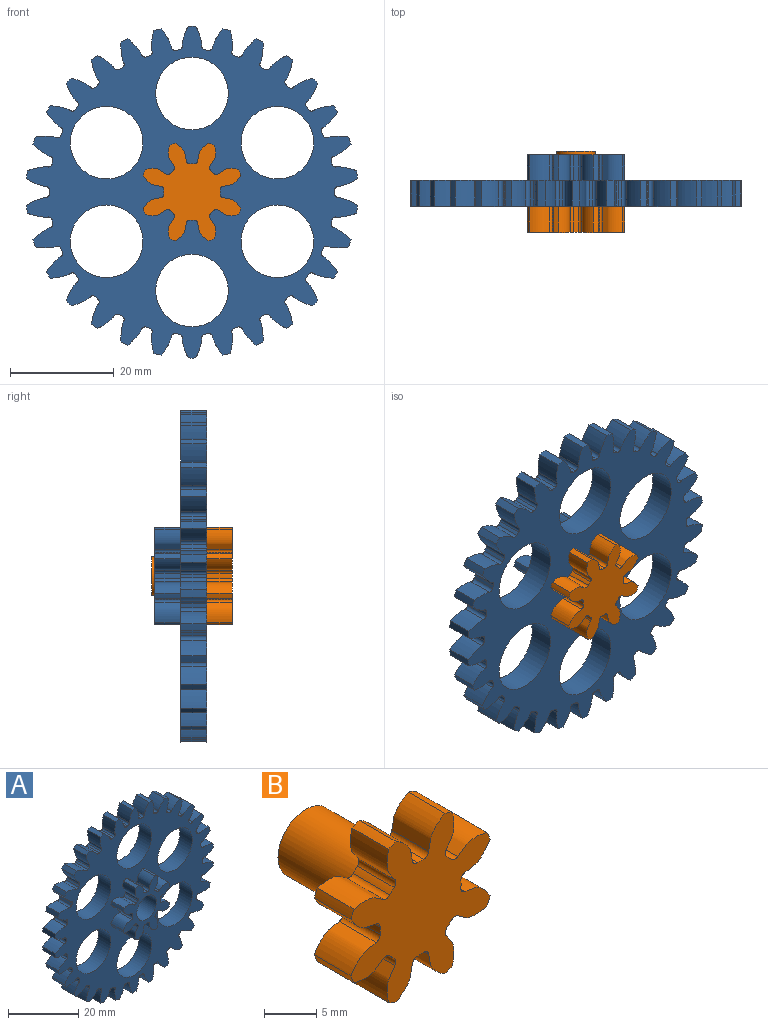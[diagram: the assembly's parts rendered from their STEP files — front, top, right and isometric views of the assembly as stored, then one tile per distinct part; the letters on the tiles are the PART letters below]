
ASSEMBLY  parts=2 mates=1
PART A: 238 faces, bbox 63.8x10x64 mm
  f0: extruded ~5x3.41mm, area 21.2mm2, adj f31,f32,f33,f49
  f1: cylinder r=5.5mm len=5mm, axis (0,1,0), area 4.1mm2, adj f32,f33,f34,f49
  f2: extruded ~5x3.41mm, area 21.2mm2, adj f3,f32,f34,f49
  f3: cylinder r=10mm len=5mm, axis (0,1,0), area 5.4mm2, adj f2,f4,f32,f49
  f4: extruded ~5x3.98mm, area 21.2mm2, adj f3,f32,f35,f49
  f5: cylinder r=5.5mm len=5mm, axis (0,1,0), area 4.1mm2, adj f32,f35,f36,f49
  f6: extruded ~5x3.98mm, area 21.2mm2, adj f7,f32,f36,f49
  f7: cylinder r=10mm len=5mm, axis (0,1,0), area 5.4mm2, adj f6,f8,f32,f49
  f8: extruded ~5x3.41mm, area 21.2mm2, adj f7,f32,f37,f49
  f9: cylinder r=5.5mm len=5mm, axis (0,1,0), area 4.1mm2, adj f32,f37,f38,f49
  f10: extruded ~5x3.41mm, area 21.2mm2, adj f11,f32,f38,f49
  f11: cylinder r=10mm len=5mm, axis (0,1,0), area 5.4mm2, adj f10,f12,f32,f49
  f12: extruded ~5x3.98mm, area 21.2mm2, adj f11,f32,f39,f49
  f13: cylinder r=5.5mm len=5mm, axis (0,1,0), area 4.1mm2, adj f32,f39,f40,f49
  f14: extruded ~5x3.98mm, area 21.2mm2, adj f15,f32,f40,f49
  f15: cylinder r=10mm len=5mm, axis (0,1,0), area 5.4mm2, adj f14,f16,f32,f49
  f16: extruded ~5x3.41mm, area 21.2mm2, adj f15,f32,f41,f49
  f17: cylinder r=5.5mm len=5mm, axis (0,1,0), area 4.1mm2, adj f32,f41,f42,f49
  f18: extruded ~5x3.41mm, area 21.2mm2, adj f19,f32,f42,f49
  f19: cylinder r=10mm len=5mm, axis (0,1,0), area 5.4mm2, adj f18,f20,f32,f49
  f20: extruded ~5x3.98mm, area 21.2mm2, adj f19,f32,f43,f49
  f21: cylinder r=5.5mm len=5mm, axis (0,1,0), area 4.1mm2, adj f32,f43,f44,f49
  f22: extruded ~5x3.98mm, area 21.2mm2, adj f23,f32,f44,f49
  f23: cylinder r=10mm len=5mm, axis (0,1,0), area 5.4mm2, adj f22,f24,f32,f49
  f24: extruded ~5x3.41mm, area 21.2mm2, adj f23,f32,f45,f49
  f25: cylinder r=5.5mm len=5mm, axis (0,1,0), area 4.1mm2, adj f32,f45,f46,f49
  f26: extruded ~5x3.41mm, area 21.2mm2, adj f27,f32,f46,f49
  f27: cylinder r=10mm len=5mm, axis (0,1,0), area 5.4mm2, adj f26,f28,f32,f49
  f28: extruded ~5x3.98mm, area 21.2mm2, adj f27,f32,f47,f49
  f29: cylinder r=5.5mm len=5mm, axis (0,1,0), area 4.1mm2, adj f32,f47,f48,f49
  f30: extruded ~5x3.98mm, area 21.2mm2, adj f31,f32,f48,f49
  f31: cylinder r=10mm len=5mm, axis (0,1,0), area 5.4mm2, adj f0,f30,f32,f49
  f32: plane 18.97x18.97mm, normal (0,-1,0), area 140mm2, adj f0,f1,f2,f3,f4,f5,f6,f7
  f33: cylinder r=0.66mm len=5mm, axis (0,1,0), area 4.8mm2, adj f0,f1,f32,f49
  f34: cylinder r=0.66mm len=5mm, axis (0,1,0), area 4.8mm2, adj f1,f2,f32,f49
  f35: cylinder r=0.66mm len=5mm, axis (0,1,0), area 4.8mm2, adj f4,f5,f32,f49
  f36: cylinder r=0.66mm len=5mm, axis (0,1,0), area 4.8mm2, adj f5,f6,f32,f49
  f37: cylinder r=0.66mm len=5mm, axis (0,1,0), area 4.8mm2, adj f8,f9,f32,f49
  f38: cylinder r=0.66mm len=5mm, axis (0,1,0), area 4.8mm2, adj f9,f10,f32,f49
  f39: cylinder r=0.66mm len=5mm, axis (0,1,0), area 4.8mm2, adj f12,f13,f32,f49
  f40: cylinder r=0.66mm len=5mm, axis (0,1,0), area 4.8mm2, adj f13,f14,f32,f49
  f41: cylinder r=0.66mm len=5mm, axis (0,1,0), area 4.8mm2, adj f16,f17,f32,f49
  f42: cylinder r=0.66mm len=5mm, axis (0,1,0), area 4.8mm2, adj f17,f18,f32,f49
  f43: cylinder r=0.66mm len=5mm, axis (0,1,0), area 4.8mm2, adj f20,f21,f32,f49
  f44: cylinder r=0.66mm len=5mm, axis (0,1,0), area 4.8mm2, adj f21,f22,f32,f49
  f45: cylinder r=0.66mm len=5mm, axis (0,1,0), area 4.8mm2, adj f24,f25,f32,f49
  f46: cylinder r=0.66mm len=5mm, axis (0,1,0), area 4.8mm2, adj f25,f26,f32,f49
  f47: cylinder r=0.66mm len=5mm, axis (0,1,0), area 4.8mm2, adj f28,f29,f32,f49
  f48: cylinder r=0.66mm len=5mm, axis (0,1,0), area 4.8mm2, adj f29,f30,f32,f49
  f49: plane 64x63.79mm, normal (0,-1,0), area 1681.1mm2, adj f0,f1,f2,f3,f4,f5,f6,f7
  f50: extruded ~5x3.75mm, area 20.5mm2, adj f49,f169,f170,f230
  f51: cylinder r=27.5mm len=5mm, axis (0,1,0), area 3.6mm2, adj f49,f170,f171,f230
  f52: extruded ~5x3.75mm, area 20.5mm2, adj f49,f53,f171,f230
  f53: cylinder r=32mm len=5mm, axis (0,1,0), area 7.4mm2, adj f49,f52,f54,f230
  f54: extruded ~5x3.99mm, area 20.5mm2, adj f49,f53,f172,f230
  f55: cylinder r=27.5mm len=5mm, axis (0,1,0), area 3.6mm2, adj f49,f172,f173,f230
  f56: extruded ~5x3.34mm, area 20.5mm2, adj f49,f57,f173,f230
  f57: cylinder r=32mm len=5mm, axis (0,1,0), area 7.4mm2, adj f49,f56,f58,f230
  f58: extruded ~5x4.06mm, area 20.5mm2, adj f49,f57,f174,f230
  f59: cylinder r=27.5mm len=5mm, axis (0,1,0), area 3.6mm2, adj f49,f174,f175,f230
  f60: extruded ~5x2.95mm, area 20.5mm2, adj f49,f61,f175,f230
  f61: cylinder r=32mm len=5mm, axis (0,1,0), area 7.4mm2, adj f49,f60,f62,f230
  f62: extruded ~5x3.95mm, area 20.5mm2, adj f49,f61,f176,f230
  f63: cylinder r=27.5mm len=5mm, axis (0,1,0), area 3.6mm2, adj f49,f176,f177,f230
  f64: extruded ~5x3.46mm, area 20.5mm2, adj f49,f65,f177,f230
  f65: cylinder r=32mm len=5mm, axis (0,1,0), area 7.4mm2, adj f49,f64,f66,f230
  f66: extruded ~5x3.67mm, area 20.5mm2, adj f49,f65,f178,f230
  f67: cylinder r=27.5mm len=5mm, axis (0,1,0), area 3.6mm2, adj f49,f178,f179,f230
  f68: extruded ~5x3.83mm, area 20.5mm2, adj f49,f69,f179,f230
  f69: cylinder r=32mm len=5mm, axis (0,1,0), area 7.4mm2, adj f49,f68,f70,f230
  f70: extruded ~5x3.22mm, area 20.5mm2, adj f49,f69,f180,f230
  f71: cylinder r=27.5mm len=5mm, axis (0,1,0), area 3.6mm2, adj f49,f180,f181,f230
  f72: extruded ~5x4.02mm, area 20.5mm2, adj f49,f73,f181,f230
  f73: cylinder r=32mm len=5mm, axis (0,1,0), area 7.4mm2, adj f49,f72,f74,f230
  f74: extruded ~5x3.08mm, area 20.5mm2, adj f49,f73,f182,f230
  f75: cylinder r=27.5mm len=5mm, axis (0,1,0), area 3.6mm2, adj f49,f182,f183,f230
  f76: extruded ~5x4.04mm, area 20.5mm2, adj f49,f77,f183,f230
  f77: cylinder r=32mm len=5mm, axis (0,1,0), area 7.4mm2, adj f49,f76,f78,f230
  f78: extruded ~5x3.56mm, area 20.5mm2, adj f49,f77,f184,f230
  f79: cylinder r=27.5mm len=5mm, axis (0,1,0), area 3.6mm2, adj f49,f184,f185,f230
  f80: extruded ~5x3.89mm, area 20.5mm2, adj f49,f81,f185,f230
  f81: cylinder r=32mm len=5mm, axis (0,1,0), area 7.4mm2, adj f49,f80,f82,f230
  f82: extruded ~5x3.89mm, area 20.5mm2, adj f49,f81,f186,f230
  f83: cylinder r=27.5mm len=5mm, axis (0,1,0), area 3.6mm2, adj f49,f186,f187,f230
  f84: extruded ~5x3.56mm, area 20.5mm2, adj f49,f85,f187,f230
  f85: cylinder r=32mm len=5mm, axis (0,1,0), area 7.4mm2, adj f49,f84,f86,f230
  f86: extruded ~5x4.04mm, area 20.5mm2, adj f49,f85,f188,f230
  f87: cylinder r=27.5mm len=5mm, axis (0,1,0), area 3.6mm2, adj f49,f188,f189,f230
  f88: extruded ~5x3.08mm, area 20.5mm2, adj f49,f89,f189,f230
  f89: cylinder r=32mm len=5mm, axis (0,1,0), area 7.4mm2, adj f49,f88,f90,f230
  f90: extruded ~5x4.02mm, area 20.5mm2, adj f49,f89,f190,f230
  f91: cylinder r=27.5mm len=5mm, axis (0,1,0), area 3.6mm2, adj f49,f190,f191,f230
  f92: extruded ~5x3.22mm, area 20.5mm2, adj f49,f93,f191,f230
  f93: cylinder r=32mm len=5mm, axis (0,1,0), area 7.4mm2, adj f49,f92,f94,f230
  f94: extruded ~5x3.83mm, area 20.5mm2, adj f49,f93,f192,f230
  f95: cylinder r=27.5mm len=5mm, axis (0,1,0), area 3.6mm2, adj f49,f192,f193,f230
  f96: extruded ~5x3.67mm, area 20.5mm2, adj f49,f97,f193,f230
  f97: cylinder r=32mm len=5mm, axis (0,1,0), area 7.4mm2, adj f49,f96,f98,f230
  f98: extruded ~5x3.46mm, area 20.5mm2, adj f49,f97,f194,f230
  f99: cylinder r=27.5mm len=5mm, axis (0,1,0), area 3.6mm2, adj f49,f194,f195,f230
  f100: extruded ~5x3.95mm, area 20.5mm2, adj f49,f101,f195,f230
  f101: cylinder r=32mm len=5mm, axis (0,1,0), area 7.4mm2, adj f49,f100,f102,f230
  f102: extruded ~5x2.95mm, area 20.5mm2, adj f49,f101,f196,f230
  f103: cylinder r=27.5mm len=5mm, axis (0,1,0), area 3.6mm2, adj f49,f196,f197,f230
  f104: extruded ~5x4.06mm, area 20.5mm2, adj f49,f105,f197,f230
  f105: cylinder r=32mm len=5mm, axis (0,1,0), area 7.4mm2, adj f49,f104,f106,f230
  f106: extruded ~5x3.34mm, area 20.5mm2, adj f49,f105,f198,f230
  f107: cylinder r=27.5mm len=5mm, axis (0,1,0), area 3.6mm2, adj f49,f198,f199,f230
  f108: extruded ~5x3.99mm, area 20.5mm2, adj f49,f109,f199,f230
  f109: cylinder r=32mm len=5mm, axis (0,1,0), area 7.4mm2, adj f49,f108,f110,f230
  f110: extruded ~5x3.75mm, area 20.5mm2, adj f49,f109,f200,f230
  f111: cylinder r=27.5mm len=5mm, axis (0,1,0), area 3.6mm2, adj f49,f200,f201,f230
  f112: extruded ~5x3.75mm, area 20.5mm2, adj f49,f113,f201,f230
  f113: cylinder r=32mm len=5mm, axis (0,1,0), area 7.4mm2, adj f49,f112,f114,f230
  f114: extruded ~5x3.99mm, area 20.5mm2, adj f49,f113,f202,f230
  f115: cylinder r=27.5mm len=5mm, axis (0,1,0), area 3.6mm2, adj f49,f202,f203,f230
  f116: extruded ~5x3.34mm, area 20.5mm2, adj f49,f117,f203,f230
  f117: cylinder r=32mm len=5mm, axis (0,1,0), area 7.4mm2, adj f49,f116,f118,f230
  f118: extruded ~5x4.06mm, area 20.5mm2, adj f49,f117,f204,f230
  f119: cylinder r=27.5mm len=5mm, axis (0,1,0), area 3.6mm2, adj f49,f204,f205,f230
  f120: extruded ~5x2.95mm, area 20.5mm2, adj f49,f121,f205,f230
  f121: cylinder r=32mm len=5mm, axis (0,1,0), area 7.4mm2, adj f49,f120,f122,f230
  f122: extruded ~5x3.95mm, area 20.5mm2, adj f49,f121,f206,f230
  f123: cylinder r=27.5mm len=5mm, axis (0,1,0), area 3.6mm2, adj f49,f206,f207,f230
  f124: extruded ~5x3.46mm, area 20.5mm2, adj f49,f125,f207,f230
  f125: cylinder r=32mm len=5mm, axis (0,1,0), area 7.4mm2, adj f49,f124,f126,f230
  f126: extruded ~5x3.67mm, area 20.5mm2, adj f49,f125,f208,f230
  f127: cylinder r=27.5mm len=5mm, axis (0,1,0), area 3.6mm2, adj f49,f208,f209,f230
  f128: extruded ~5x3.83mm, area 20.5mm2, adj f49,f129,f209,f230
  f129: cylinder r=32mm len=5mm, axis (0,1,0), area 7.4mm2, adj f49,f128,f130,f230
  f130: extruded ~5x3.22mm, area 20.5mm2, adj f49,f129,f210,f230
  f131: cylinder r=27.5mm len=5mm, axis (0,1,0), area 3.6mm2, adj f49,f210,f211,f230
  f132: extruded ~5x4.02mm, area 20.5mm2, adj f49,f133,f211,f230
  f133: cylinder r=32mm len=5mm, axis (0,1,0), area 7.4mm2, adj f49,f132,f134,f230
  f134: extruded ~5x3.08mm, area 20.5mm2, adj f49,f133,f212,f230
  f135: cylinder r=27.5mm len=5mm, axis (0,1,0), area 3.6mm2, adj f49,f212,f213,f230
  f136: extruded ~5x4.04mm, area 20.5mm2, adj f49,f137,f213,f230
  f137: cylinder r=32mm len=5mm, axis (0,1,0), area 7.4mm2, adj f49,f136,f138,f230
  f138: extruded ~5x3.56mm, area 20.5mm2, adj f49,f137,f214,f230
  f139: cylinder r=27.5mm len=5mm, axis (0,1,0), area 3.6mm2, adj f49,f214,f215,f230
  f140: extruded ~5x3.89mm, area 20.5mm2, adj f49,f141,f215,f230
  f141: cylinder r=32mm len=5mm, axis (0,1,0), area 7.4mm2, adj f49,f140,f142,f230
  f142: extruded ~5x3.89mm, area 20.5mm2, adj f49,f141,f216,f230
  f143: cylinder r=27.5mm len=5mm, axis (0,1,0), area 3.6mm2, adj f49,f216,f217,f230
  f144: extruded ~5x3.56mm, area 20.5mm2, adj f49,f145,f217,f230
  f145: cylinder r=32mm len=5mm, axis (0,1,0), area 7.4mm2, adj f49,f144,f146,f230
  f146: extruded ~5x4.04mm, area 20.5mm2, adj f49,f145,f218,f230
  f147: cylinder r=27.5mm len=5mm, axis (0,1,0), area 3.6mm2, adj f49,f218,f219,f230
  f148: extruded ~5x3.08mm, area 20.5mm2, adj f49,f149,f219,f230
  f149: cylinder r=32mm len=5mm, axis (0,1,0), area 7.4mm2, adj f49,f148,f150,f230
  f150: extruded ~5x4.02mm, area 20.5mm2, adj f49,f149,f220,f230
  f151: cylinder r=27.5mm len=5mm, axis (0,1,0), area 3.6mm2, adj f49,f220,f221,f230
  f152: extruded ~5x3.22mm, area 20.5mm2, adj f49,f153,f221,f230
  f153: cylinder r=32mm len=5mm, axis (0,1,0), area 7.4mm2, adj f49,f152,f154,f230
  f154: extruded ~5x3.83mm, area 20.5mm2, adj f49,f153,f222,f230
  f155: cylinder r=27.5mm len=5mm, axis (0,1,0), area 3.6mm2, adj f49,f222,f223,f230
  f156: extruded ~5x3.67mm, area 20.5mm2, adj f49,f157,f223,f230
  f157: cylinder r=32mm len=5mm, axis (0,1,0), area 7.4mm2, adj f49,f156,f158,f230
  f158: extruded ~5x3.46mm, area 20.5mm2, adj f49,f157,f224,f230
  f159: cylinder r=27.5mm len=5mm, axis (0,1,0), area 3.6mm2, adj f49,f224,f225,f230
  f160: extruded ~5x3.95mm, area 20.5mm2, adj f49,f161,f225,f230
  f161: cylinder r=32mm len=5mm, axis (0,1,0), area 7.4mm2, adj f49,f160,f162,f230
  f162: extruded ~5x2.95mm, area 20.5mm2, adj f49,f161,f226,f230
  f163: cylinder r=27.5mm len=5mm, axis (0,1,0), area 3.6mm2, adj f49,f226,f227,f230
  f164: extruded ~5x4.06mm, area 20.5mm2, adj f49,f165,f227,f230
  f165: cylinder r=32mm len=5mm, axis (0,1,0), area 7.4mm2, adj f49,f164,f166,f230
  f166: extruded ~5x3.34mm, area 20.5mm2, adj f49,f165,f228,f230
  f167: cylinder r=27.5mm len=5mm, axis (0,1,0), area 3.6mm2, adj f49,f228,f229,f230
  f168: extruded ~5x3.99mm, area 20.5mm2, adj f49,f169,f229,f230
  f169: cylinder r=32mm len=5mm, axis (0,1,0), area 7.4mm2, adj f49,f50,f168,f230
  f170: cylinder r=0.69mm len=5mm, axis (0,1,0), area 5.2mm2, adj f49,f50,f51,f230
  f171: cylinder r=0.69mm len=5mm, axis (0,1,0), area 5.2mm2, adj f49,f51,f52,f230
  f172: cylinder r=0.69mm len=5mm, axis (0,1,0), area 5.2mm2, adj f49,f54,f55,f230
  f173: cylinder r=0.69mm len=5mm, axis (0,1,0), area 5.2mm2, adj f49,f55,f56,f230
  f174: cylinder r=0.69mm len=5mm, axis (0,1,0), area 5.2mm2, adj f49,f58,f59,f230
  f175: cylinder r=0.69mm len=5mm, axis (0,1,0), area 5.2mm2, adj f49,f59,f60,f230
  f176: cylinder r=0.69mm len=5mm, axis (0,1,0), area 5.2mm2, adj f49,f62,f63,f230
  f177: cylinder r=0.69mm len=5mm, axis (0,1,0), area 5.2mm2, adj f49,f63,f64,f230
  f178: cylinder r=0.69mm len=5mm, axis (0,1,0), area 5.2mm2, adj f49,f66,f67,f230
  f179: cylinder r=0.69mm len=5mm, axis (0,1,0), area 5.2mm2, adj f49,f67,f68,f230
  f180: cylinder r=0.69mm len=5mm, axis (0,1,0), area 5.2mm2, adj f49,f70,f71,f230
  f181: cylinder r=0.69mm len=5mm, axis (0,1,0), area 5.2mm2, adj f49,f71,f72,f230
  f182: cylinder r=0.69mm len=5mm, axis (0,1,0), area 5.2mm2, adj f49,f74,f75,f230
  f183: cylinder r=0.69mm len=5mm, axis (0,1,0), area 5.2mm2, adj f49,f75,f76,f230
  f184: cylinder r=0.69mm len=5mm, axis (0,1,0), area 5.2mm2, adj f49,f78,f79,f230
  f185: cylinder r=0.69mm len=5mm, axis (0,1,0), area 5.2mm2, adj f49,f79,f80,f230
  f186: cylinder r=0.69mm len=5mm, axis (0,1,0), area 5.2mm2, adj f49,f82,f83,f230
  f187: cylinder r=0.69mm len=5mm, axis (0,1,0), area 5.2mm2, adj f49,f83,f84,f230
  f188: cylinder r=0.69mm len=5mm, axis (0,1,0), area 5.2mm2, adj f49,f86,f87,f230
  f189: cylinder r=0.69mm len=5mm, axis (0,1,0), area 5.2mm2, adj f49,f87,f88,f230
  f190: cylinder r=0.69mm len=5mm, axis (0,1,0), area 5.2mm2, adj f49,f90,f91,f230
  f191: cylinder r=0.69mm len=5mm, axis (0,1,0), area 5.2mm2, adj f49,f91,f92,f230
  f192: cylinder r=0.69mm len=5mm, axis (0,1,0), area 5.2mm2, adj f49,f94,f95,f230
  f193: cylinder r=0.69mm len=5mm, axis (0,1,0), area 5.2mm2, adj f49,f95,f96,f230
  f194: cylinder r=0.69mm len=5mm, axis (0,1,0), area 5.2mm2, adj f49,f98,f99,f230
  f195: cylinder r=0.69mm len=5mm, axis (0,1,0), area 5.2mm2, adj f49,f99,f100,f230
  f196: cylinder r=0.69mm len=5mm, axis (0,1,0), area 5.2mm2, adj f49,f102,f103,f230
  f197: cylinder r=0.69mm len=5mm, axis (0,1,0), area 5.2mm2, adj f49,f103,f104,f230
  f198: cylinder r=0.69mm len=5mm, axis (0,1,0), area 5.2mm2, adj f49,f106,f107,f230
  f199: cylinder r=0.69mm len=5mm, axis (0,1,0), area 5.2mm2, adj f49,f107,f108,f230
  f200: cylinder r=0.69mm len=5mm, axis (0,1,0), area 5.2mm2, adj f49,f110,f111,f230
  f201: cylinder r=0.69mm len=5mm, axis (0,1,0), area 5.2mm2, adj f49,f111,f112,f230
  f202: cylinder r=0.69mm len=5mm, axis (0,1,0), area 5.2mm2, adj f49,f114,f115,f230
  f203: cylinder r=0.69mm len=5mm, axis (0,1,0), area 5.2mm2, adj f49,f115,f116,f230
  f204: cylinder r=0.69mm len=5mm, axis (0,1,0), area 5.2mm2, adj f49,f118,f119,f230
  f205: cylinder r=0.69mm len=5mm, axis (0,1,0), area 5.2mm2, adj f49,f119,f120,f230
  f206: cylinder r=0.69mm len=5mm, axis (0,1,0), area 5.2mm2, adj f49,f122,f123,f230
  f207: cylinder r=0.69mm len=5mm, axis (0,1,0), area 5.2mm2, adj f49,f123,f124,f230
  f208: cylinder r=0.69mm len=5mm, axis (0,1,0), area 5.2mm2, adj f49,f126,f127,f230
  f209: cylinder r=0.69mm len=5mm, axis (0,1,0), area 5.2mm2, adj f49,f127,f128,f230
  f210: cylinder r=0.69mm len=5mm, axis (0,1,0), area 5.2mm2, adj f49,f130,f131,f230
  f211: cylinder r=0.69mm len=5mm, axis (0,1,0), area 5.2mm2, adj f49,f131,f132,f230
  f212: cylinder r=0.69mm len=5mm, axis (0,1,0), area 5.2mm2, adj f49,f134,f135,f230
  f213: cylinder r=0.69mm len=5mm, axis (0,1,0), area 5.2mm2, adj f49,f135,f136,f230
  f214: cylinder r=0.69mm len=5mm, axis (0,1,0), area 5.2mm2, adj f49,f138,f139,f230
  f215: cylinder r=0.69mm len=5mm, axis (0,1,0), area 5.2mm2, adj f49,f139,f140,f230
  f216: cylinder r=0.69mm len=5mm, axis (0,1,0), area 5.2mm2, adj f49,f142,f143,f230
  f217: cylinder r=0.69mm len=5mm, axis (0,1,0), area 5.2mm2, adj f49,f143,f144,f230
  f218: cylinder r=0.69mm len=5mm, axis (0,1,0), area 5.2mm2, adj f49,f146,f147,f230
  f219: cylinder r=0.69mm len=5mm, axis (0,1,0), area 5.2mm2, adj f49,f147,f148,f230
  f220: cylinder r=0.69mm len=5mm, axis (0,1,0), area 5.2mm2, adj f49,f150,f151,f230
  f221: cylinder r=0.69mm len=5mm, axis (0,1,0), area 5.2mm2, adj f49,f151,f152,f230
  f222: cylinder r=0.69mm len=5mm, axis (0,1,0), area 5.2mm2, adj f49,f154,f155,f230
  f223: cylinder r=0.69mm len=5mm, axis (0,1,0), area 5.2mm2, adj f49,f155,f156,f230
  f224: cylinder r=0.69mm len=5mm, axis (0,1,0), area 5.2mm2, adj f49,f158,f159,f230
  f225: cylinder r=0.69mm len=5mm, axis (0,1,0), area 5.2mm2, adj f49,f159,f160,f230
  f226: cylinder r=0.69mm len=5mm, axis (0,1,0), area 5.2mm2, adj f49,f162,f163,f230
  f227: cylinder r=0.69mm len=5mm, axis (0,1,0), area 5.2mm2, adj f49,f163,f164,f230
  f228: cylinder r=0.69mm len=5mm, axis (0,1,0), area 5.2mm2, adj f49,f166,f167,f230
  f229: cylinder r=0.69mm len=5mm, axis (0,1,0), area 5.2mm2, adj f49,f167,f168,f230
  f230: plane 64x63.79mm, normal (0,1,0), area 1821.1mm2, adj f50,f51,f52,f53,f54,f55,f56,f57
  f231: cylinder r=7mm len=14mm, axis (0,-1,0), area 219.9mm2, adj f49,f230
  f232: cylinder r=7mm len=14mm, axis (0,-1,0), area 219.9mm2, adj f49,f230
  f233: cylinder r=7mm len=14mm, axis (0,-1,0), area 219.9mm2, adj f49,f230
  f234: cylinder r=7mm len=14mm, axis (0,-1,0), area 219.9mm2, adj f49,f230
  f235: cylinder r=7mm len=14mm, axis (0,-1,0), area 219.9mm2, adj f49,f230
  f236: cylinder r=7mm len=14mm, axis (0,-1,0), area 219.9mm2, adj f49,f230
  f237: cylinder r=4mm len=10mm, axis (0,-1,0), area 251.3mm2, adj f32,f230
PART B: 52 faces, bbox 19x15.6x19 mm
  f0: extruded ~5x3.41mm, area 21.2mm2, adj f31,f32,f33,f34
  f1: cylinder r=5.5mm len=5mm, axis (0,1,0), area 4.1mm2, adj f32,f33,f34,f35
  f2: extruded ~5x3.41mm, area 21.2mm2, adj f3,f32,f33,f35
  f3: cylinder r=10mm len=5mm, axis (0,1,0), area 5.4mm2, adj f2,f4,f32,f33
  f4: extruded ~5x3.98mm, area 21.2mm2, adj f3,f32,f33,f36
  f5: cylinder r=5.5mm len=5mm, axis (0,1,0), area 4.1mm2, adj f32,f33,f36,f37
  f6: extruded ~5x3.98mm, area 21.2mm2, adj f7,f32,f33,f37
  f7: cylinder r=10mm len=5mm, axis (0,1,0), area 5.4mm2, adj f6,f8,f32,f33
  f8: extruded ~5x3.41mm, area 21.2mm2, adj f7,f32,f33,f38
  f9: cylinder r=5.5mm len=5mm, axis (0,1,0), area 4.1mm2, adj f32,f33,f38,f39
  f10: extruded ~5x3.41mm, area 21.2mm2, adj f11,f32,f33,f39
  f11: cylinder r=10mm len=5mm, axis (0,1,0), area 5.4mm2, adj f10,f12,f32,f33
  f12: extruded ~5x3.98mm, area 21.2mm2, adj f11,f32,f33,f40
  f13: cylinder r=5.5mm len=5mm, axis (0,1,0), area 4.1mm2, adj f32,f33,f40,f41
  f14: extruded ~5x3.98mm, area 21.2mm2, adj f15,f32,f33,f41
  f15: cylinder r=10mm len=5mm, axis (0,1,0), area 5.4mm2, adj f14,f16,f32,f33
  f16: extruded ~5x3.41mm, area 21.2mm2, adj f15,f32,f33,f42
  f17: cylinder r=5.5mm len=5mm, axis (0,1,0), area 4.1mm2, adj f32,f33,f42,f43
  f18: extruded ~5x3.41mm, area 21.2mm2, adj f19,f32,f33,f43
  f19: cylinder r=10mm len=5mm, axis (0,1,0), area 5.4mm2, adj f18,f20,f32,f33
  f20: extruded ~5x3.98mm, area 21.2mm2, adj f19,f32,f33,f44
  f21: cylinder r=5.5mm len=5mm, axis (0,1,0), area 4.1mm2, adj f32,f33,f44,f45
  f22: extruded ~5x3.98mm, area 21.2mm2, adj f23,f32,f33,f45
  f23: cylinder r=10mm len=5mm, axis (0,1,0), area 5.4mm2, adj f22,f24,f32,f33
  f24: extruded ~5x3.41mm, area 21.2mm2, adj f23,f32,f33,f46
  f25: cylinder r=5.5mm len=5mm, axis (0,1,0), area 4.1mm2, adj f32,f33,f46,f47
  f26: extruded ~5x3.41mm, area 21.2mm2, adj f27,f32,f33,f47
  f27: cylinder r=10mm len=5mm, axis (0,1,0), area 5.4mm2, adj f26,f28,f32,f33
  f28: extruded ~5x3.98mm, area 21.2mm2, adj f27,f32,f33,f48
  f29: cylinder r=5.5mm len=5mm, axis (0,1,0), area 4.1mm2, adj f32,f33,f48,f49
  f30: extruded ~5x3.98mm, area 21.2mm2, adj f31,f32,f33,f49
  f31: cylinder r=10mm len=5mm, axis (0,1,0), area 5.4mm2, adj f0,f30,f32,f33
  f32: plane 18.97x18.97mm, normal (0,-1,0), area 190.3mm2, adj f0,f1,f2,f3,f4,f5,f6,f7
  f33: plane 18.97x18.97mm, normal (0,1,0), area 146.1mm2, adj f0,f1,f2,f3,f4,f5,f6,f7
  f34: cylinder r=0.66mm len=5mm, axis (0,1,0), area 4.8mm2, adj f0,f1,f32,f33
  f35: cylinder r=0.66mm len=5mm, axis (0,1,0), area 4.8mm2, adj f1,f2,f32,f33
  f36: cylinder r=0.66mm len=5mm, axis (0,1,0), area 4.8mm2, adj f4,f5,f32,f33
  f37: cylinder r=0.66mm len=5mm, axis (0,1,0), area 4.8mm2, adj f5,f6,f32,f33
  f38: cylinder r=0.66mm len=5mm, axis (0,1,0), area 4.8mm2, adj f8,f9,f32,f33
  f39: cylinder r=0.66mm len=5mm, axis (0,1,0), area 4.8mm2, adj f9,f10,f32,f33
  f40: cylinder r=0.66mm len=5mm, axis (0,1,0), area 4.8mm2, adj f12,f13,f32,f33
  f41: cylinder r=0.66mm len=5mm, axis (0,1,0), area 4.8mm2, adj f13,f14,f32,f33
  f42: cylinder r=0.66mm len=5mm, axis (0,1,0), area 4.8mm2, adj f16,f17,f32,f33
  f43: cylinder r=0.66mm len=5mm, axis (0,1,0), area 4.8mm2, adj f17,f18,f32,f33
  f44: cylinder r=0.66mm len=5mm, axis (0,1,0), area 4.8mm2, adj f20,f21,f32,f33
  f45: cylinder r=0.66mm len=5mm, axis (0,1,0), area 4.8mm2, adj f21,f22,f32,f33
  f46: cylinder r=0.66mm len=5mm, axis (0,1,0), area 4.8mm2, adj f24,f25,f32,f33
  f47: cylinder r=0.66mm len=5mm, axis (0,1,0), area 4.8mm2, adj f25,f26,f32,f33
  f48: cylinder r=0.66mm len=5mm, axis (0,1,0), area 4.8mm2, adj f28,f29,f32,f33
  f49: cylinder r=0.66mm len=5mm, axis (0,1,0), area 4.8mm2, adj f29,f30,f32,f33
  f50: cylinder r=3.75mm len=10.6mm, axis (0,-1,0), area 249.8mm2, adj f33,f51
  f51: plane 7.5x7.5mm, normal (0,1,0), area 44.2mm2, adj f50
PLACE A rot(axis=(1,0,0),180deg) t=(0,0,0)mm
PLACE B at identity
MATE cylindrical A.f237 <-> B.f50  axis (0,-1,0) through (0,0,0)mm
